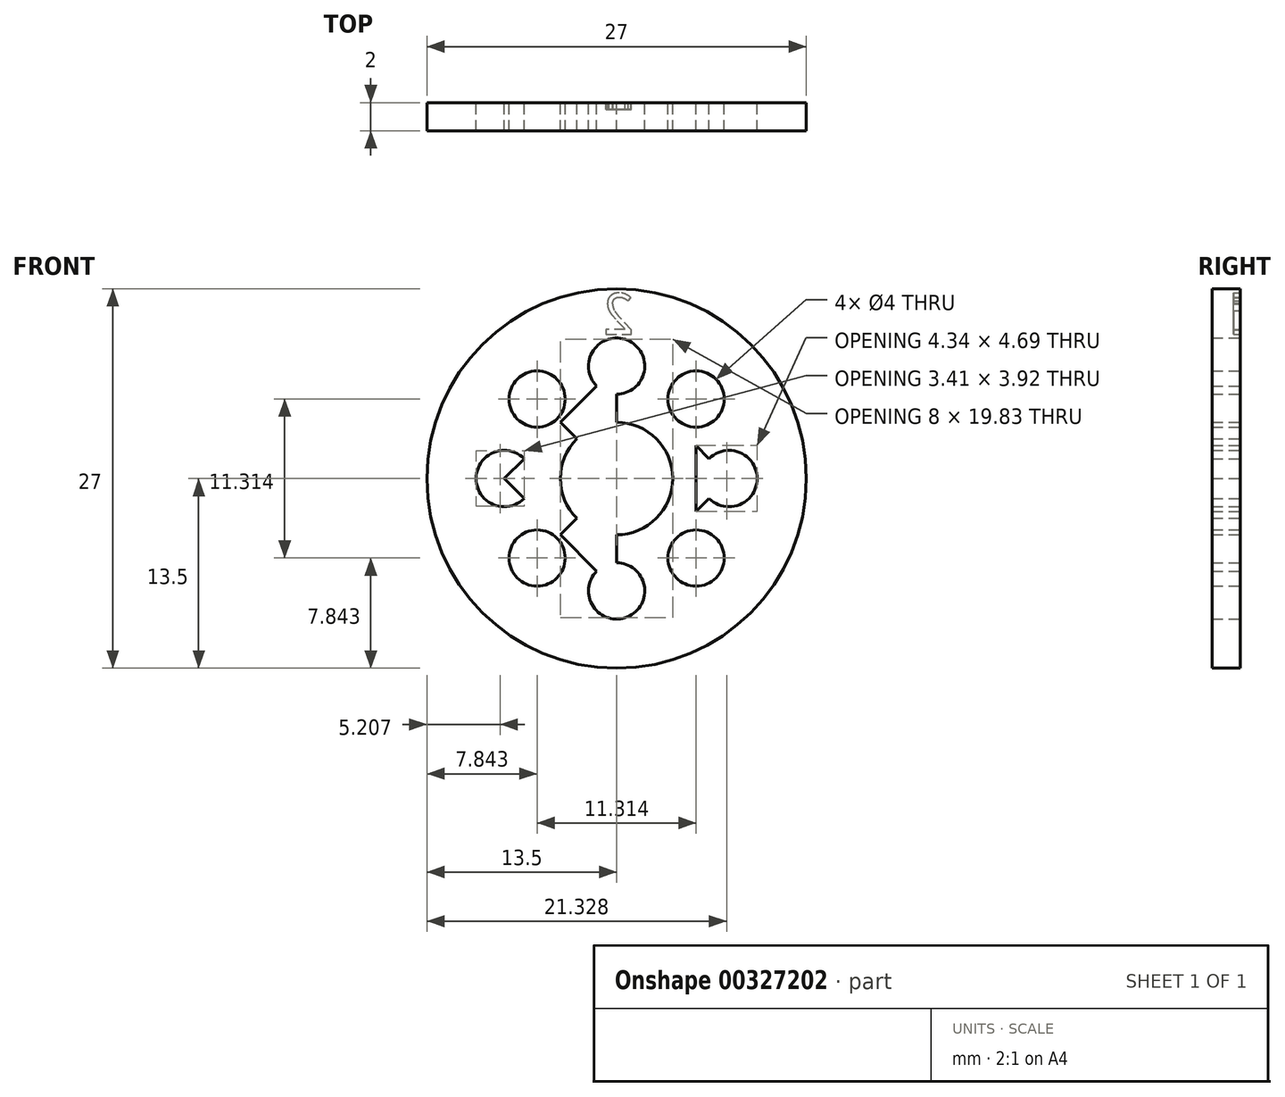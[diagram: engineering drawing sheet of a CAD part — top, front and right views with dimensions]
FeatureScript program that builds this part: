
annotation { "Feature Type Name" : "Feature", "Feature Type Description" : "" }
export const myFeature = defineFeature(function(context is Context, id is Id, definition is map)
    precondition{}
    {
        {
            var Q0;
            Q0=qCreatedBy(makeId("Front.planeOp"),FACE);
            var sketch = newSketch(context, id + "F0", { "sketchPlane" : qUnion([Q0])});
            skCircle(sketch, "E0", {"center": v(0, 0) * mm, "radius": 13.5 * mm});
            skCircle(sketch, "E1", {"center": v(0, 0) * mm, "radius": 4 * mm});
            skLineSegment(sketch, "E2", {"start": v(0, 0) * mm, "end": v(0, 8) * mm});
            skLineSegment(sketch, "E3", {"start": v(0, 8) * mm, "end": v(0, -8) * mm});
            skLineSegment(sketch, "E4", {"start": v(0, 0) * mm, "end": v(8, 0) * mm});
            skLineSegment(sketch, "E5", {"start": v(8, 0) * mm, "end": v(-8, 0) * mm});
            skLineSegment(sketch, "E6", {"start": v(-8, 0) * mm, "end": v(0, 8) * mm});
            skLineSegment(sketch, "E7", {"start": v(8, 0) * mm, "end": v(0, 8) * mm});
            skLineSegment(sketch, "E8", {"start": v(-8, 0) * mm, "end": v(0, -8) * mm});
            skLineSegment(sketch, "E9", {"start": v(0, -8) * mm, "end": v(8, 0) * mm});
            skLineSegment(sketch, "E10", {"start": v(0, 0) * mm, "end": v(-5.66, -5.66) * mm});
            skLineSegment(sketch, "E11", {"start": v(-5.66, -5.66) * mm, "end": v(5.66, 5.66) * mm});
            skLineSegment(sketch, "E12", {"start": v(5.66, 5.66) * mm, "end": v(5.66, -5.66) * mm});
            skLineSegment(sketch, "E13", {"start": v(5.66, -5.66) * mm, "end": v(-5.66, 5.66) * mm});
            skCircle(sketch, "E14", {"center": v(-5.66, 5.66) * mm, "radius": 2 * mm});
            skCircle(sketch, "E15", {"center": v(5.66, 5.66) * mm, "radius": 2 * mm});
            skCircle(sketch, "E16", {"center": v(5.66, -5.66) * mm, "radius": 2 * mm});
            skCircle(sketch, "E17", {"center": v(8, 0) * mm, "radius": 2 * mm});
            skCircle(sketch, "E18", {"center": v(0, 8) * mm, "radius": 2 * mm});
            skCircle(sketch, "E19", {"center": v(-8, 0) * mm, "radius": 2 * mm});
            skCircle(sketch, "E20", {"center": v(-5.66, -5.66) * mm, "radius": 2 * mm});
            skCircle(sketch, "E21", {"center": v(0, -8) * mm, "radius": 2 * mm});
            skSolve(sketch);
        }
        {
            var Q0;
            Q0=makeQuery(id+"F0.imprint","IMPRINT",FACE,{"disambiguationData":[TD([[makeQuery(id+"F0.imprint","IMPRINT",EDGE,{"derivedFrom":sQuery(id+"F0.wireOp",EDGE,"E0")}),1.0]])]});
            var Q1;
            {var subQ3=sQuery(id+"F0.wireOp",EDGE,"E1");var subQ7=sQuery(id+"F0.wireOp",EDGE,"E3");var subQ8=makeQuery(id+"F0.imprint","INTERSECT",VERTEX,{"disambiguationData":[OD(0.0)],"derivedFrom":[subQ3,subQ7]});Q1=makeQuery(id+"F0.imprint","IMPRINT",FACE,{"disambiguationData":[TD([[makeQuery(id+"F0.imprint","IMPRINT",EDGE,{"disambiguationData":[TD([[subQ8,-1.0]])],"derivedFrom":subQ3}),-1.0]])]});}
            var Q2;
            {var subQ0=sQuery(id+"F0.wireOp",EDGE,"E11");var subQ1=sQuery(id+"F0.wireOp",EDGE,"E1");var subQ2=makeQuery(id+"F0.imprint","INTERSECT",VERTEX,{"disambiguationData":[OD(0.0)],"derivedFrom":[subQ1,subQ0]});Q2=makeQuery(id+"F0.imprint","IMPRINT",FACE,{"disambiguationData":[TD([[makeQuery(id+"F0.imprint","IMPRINT",EDGE,{"disambiguationData":[TD([[subQ2,-1.0]])],"derivedFrom":subQ1}),-1.0]])]});}
            var Q3;
            {var subQ0=sQuery(id+"F0.wireOp",EDGE,"E13");var subQ3=sQuery(id+"F0.wireOp",EDGE,"E1");var subQ4=makeQuery(id+"F0.imprint","INTERSECT",VERTEX,{"disambiguationData":[OD(0.0)],"derivedFrom":[subQ3,subQ0]});Q3=makeQuery(id+"F0.imprint","IMPRINT",FACE,{"disambiguationData":[TD([[makeQuery(id+"F0.imprint","IMPRINT",EDGE,{"disambiguationData":[TD([[subQ4,-1.0]])],"derivedFrom":subQ3}),-1.0]])]});}
            var Q4;
            {var subQ5=sQuery(id+"F0.wireOp",EDGE,"E1");var subQ7=sQuery(id+"F0.wireOp",EDGE,"E5");var subQ8=makeQuery(id+"F0.imprint","INTERSECT",VERTEX,{"disambiguationData":[OD(1.0)],"derivedFrom":[subQ5,subQ7]});Q4=makeQuery(id+"F0.imprint","IMPRINT",FACE,{"disambiguationData":[TD([[makeQuery(id+"F0.imprint","IMPRINT",EDGE,{"disambiguationData":[TD([[subQ8,-1.0]])],"derivedFrom":subQ5}),-1.0]])]});}
            var Q5;
            {var subQ0=sQuery(id+"F0.wireOp",EDGE,"E11");var subQ3=sQuery(id+"F0.wireOp",EDGE,"E1");var subQ4=makeQuery(id+"F0.imprint","INTERSECT",VERTEX,{"disambiguationData":[OD(1.0)],"derivedFrom":[subQ3,subQ0]});Q5=makeQuery(id+"F0.imprint","IMPRINT",FACE,{"disambiguationData":[TD([[makeQuery(id+"F0.imprint","IMPRINT",EDGE,{"disambiguationData":[TD([[subQ4,-1.0]])],"derivedFrom":subQ3}),-1.0]])]});}
            var Q6;
            {var subQ1=sQuery(id+"F0.wireOp",EDGE,"E1");var subQ7=sQuery(id+"F0.wireOp",EDGE,"E3");var subQ8=makeQuery(id+"F0.imprint","INTERSECT",VERTEX,{"disambiguationData":[OD(1.0)],"derivedFrom":[subQ1,subQ7]});Q6=makeQuery(id+"F0.imprint","IMPRINT",FACE,{"disambiguationData":[TD([[makeQuery(id+"F0.imprint","IMPRINT",EDGE,{"disambiguationData":[TD([[subQ8,-1.0]])],"derivedFrom":subQ1}),-1.0]])]});}
            var Q7;
            {var subQ1=sQuery(id+"F0.wireOp",EDGE,"E5");var subQ7=sQuery(id+"F0.wireOp",EDGE,"E1");var subQ8=makeQuery(id+"F0.imprint","INTERSECT",VERTEX,{"disambiguationData":[OD(0.0)],"derivedFrom":[subQ7,subQ1]});Q7=makeQuery(id+"F0.imprint","IMPRINT",FACE,{"disambiguationData":[TD([[makeQuery(id+"F0.imprint","IMPRINT",EDGE,{"disambiguationData":[TD([[subQ8,1.0]])],"derivedFrom":subQ7}),-1.0]])]});}
            var Q8;
            {var subQ0=sQuery(id+"F0.wireOp",EDGE,"E11");var subQ1=sQuery(id+"F0.wireOp",EDGE,"E1");var subQ2=makeQuery(id+"F0.imprint","INTERSECT",VERTEX,{"disambiguationData":[OD(0.0)],"derivedFrom":[subQ1,subQ0]});Q8=makeQuery(id+"F0.imprint","IMPRINT",FACE,{"disambiguationData":[TD([[makeQuery(id+"F0.imprint","IMPRINT",EDGE,{"disambiguationData":[TD([[subQ2,1.0]])],"derivedFrom":subQ1}),-1.0]])]});}
            var Q9;
            {var subQ0=sQuery(id+"F0.wireOp",EDGE,"E17");var subQ1=sQuery(id+"F0.wireOp",EDGE,"E5");var subQ2=makeQuery(id+"F0.imprint","INTERSECT",VERTEX,{"derivedFrom":[subQ1,subQ0]});Q9=makeQuery(id+"F0.imprint","IMPRINT",FACE,{"disambiguationData":[TD([[makeQuery(id+"F0.imprint","IMPRINT",EDGE,{"disambiguationData":[TD([[subQ2,-1.0]])],"derivedFrom":subQ1}),-1.0]])]});}
            var Q10;
            {var subQ0=sQuery(id+"F0.wireOp",EDGE,"E17");var subQ1=sQuery(id+"F0.wireOp",EDGE,"E5");var subQ2=makeQuery(id+"F0.imprint","INTERSECT",VERTEX,{"derivedFrom":[subQ1,subQ0]});Q10=makeQuery(id+"F0.imprint","IMPRINT",FACE,{"disambiguationData":[TD([[makeQuery(id+"F0.imprint","IMPRINT",EDGE,{"disambiguationData":[TD([[subQ2,-1.0]])],"derivedFrom":subQ1}),1.0]])]});}
            var Q11;
            {var subQ0=sQuery(id+"F0.wireOp",EDGE,"E13");var subQ1=sQuery(id+"F0.wireOp",EDGE,"E9");var subQ2=makeQuery(id+"F0.imprint","INTERSECT",VERTEX,{"derivedFrom":[subQ1,subQ0]});Q11=makeQuery(id+"F0.imprint","IMPRINT",FACE,{"disambiguationData":[TD([[makeQuery(id+"F0.imprint","IMPRINT",EDGE,{"disambiguationData":[TD([[subQ2,-1.0]])],"derivedFrom":subQ1}),-1.0]])]});}
            var Q12;
            {var subQ0=sQuery(id+"F0.wireOp",EDGE,"E12");var subQ1=sQuery(id+"F0.wireOp",EDGE,"E7");var subQ2=makeQuery(id+"F0.imprint","INTERSECT",VERTEX,{"derivedFrom":[subQ1,subQ0]});Q12=makeQuery(id+"F0.imprint","IMPRINT",FACE,{"disambiguationData":[TD([[makeQuery(id+"F0.imprint","IMPRINT",EDGE,{"disambiguationData":[TD([[subQ2,-1.0]])],"derivedFrom":subQ1}),-1.0]])]});}
            extrude(context, id + "F1", {"entities" : qUnion([Q0, Q1, Q2, Q3, Q4, Q5, Q6, Q7, Q8, Q9, Q10, Q11, Q12]), "depth" : 2 * mm});
        }
        {
            var Q0;
            Q0=makeQuery(id+"F1.opExtrude","CAP_FACE",FACE,{"disambiguationData":[OSD([sQuery(id+"F0.wireOp",EDGE,"E0"),sQuery(id+"F0.wireOp",EDGE,"E1"),sQuery(id+"F0.wireOp",EDGE,"E14"),sQuery(id+"F0.wireOp",EDGE,"E15"),sQuery(id+"F0.wireOp",EDGE,"E16"),sQuery(id+"F0.wireOp",EDGE,"E17"),sQuery(id+"F0.wireOp",EDGE,"E18"),sQuery(id+"F0.wireOp",EDGE,"E19"),sQuery(id+"F0.wireOp",EDGE,"E20"),sQuery(id+"F0.wireOp",EDGE,"E21")])],"isStart":true});
            var sketch = newSketch(context, id + "F2", { "sketchPlane" : qUnion([Q0])});
            skText(sketch, "E22", { "text": "2", "fontName": "DroidSansMono.ttf"});
            const initialGuessF2  = {"E22": [-0.00136, 0.01027, 1, 0, 0.00293]};
            skSetInitialGuess(sketch, initialGuessF2);
            skSolve(sketch);
        }
        {
            var Q0;
            Q0=makeQuery(id+"F2.imprint","IMPRINT",FACE,{"disambiguationData":[TD([[makeQuery(id+"F2.imprint","IMPRINT",EDGE,{"derivedFrom":sQuery(id+"F2.wireOp",EDGE,"E22.sketch_text.stroke-0")}),-1.0]])]});
            extrude(context, id + "F3", {"entities" : qUnion([Q0]), "operationType" : NewBodyOperationType.REMOVE, "oppositeDirection" : true, "depth" : 0.5 * mm});
        }
    });
